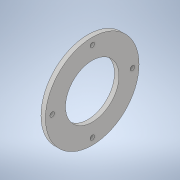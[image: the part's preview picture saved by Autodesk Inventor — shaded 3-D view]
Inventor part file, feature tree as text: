
AUTODESK INVENTOR PART (.ipt)
format: ipt  version: 2021 (Build 250183000, 183)  size: 112,640 bytes
history: native  units: in
note: dims shown in document units (in); Inventor stores cm internally (conversion verified against a paired STEP export)
features: extrude x1, sketch x1
ambient origin geometry x8: Origin, YZ Plane, XZ Plane, XY Plane, X Axis, Y Axis, Z Axis, Center Point
bodies: Body1 (feature_tree)
feature tree (2):
  extrude  "Extrusion3"  Depth=0.25in
  sketch  "Sketch3"  dims[d13=5.25in d14=0.25in d15=1.5748in d17=360.0deg d19=2.25in d20=3.0in d21=0.25in d22=0.0in]
